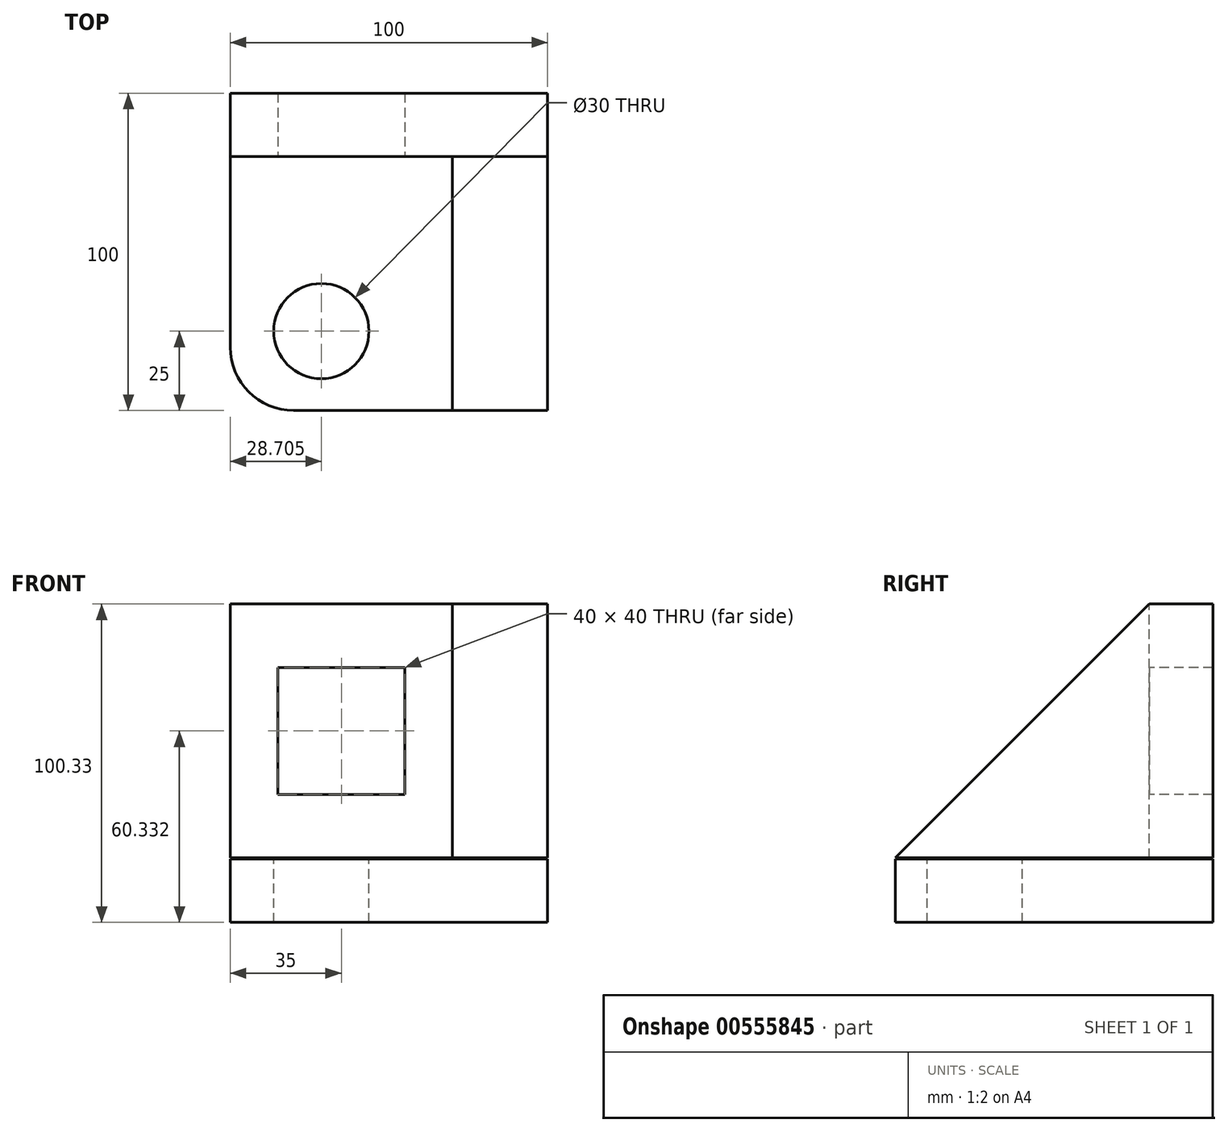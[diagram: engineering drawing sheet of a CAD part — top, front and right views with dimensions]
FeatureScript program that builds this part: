
annotation { "Feature Type Name" : "Feature", "Feature Type Description" : "" }
export const myFeature = defineFeature(function(context is Context, id is Id, definition is map)
    precondition{}
    {
        {
            var Q0;
            Q0=qCreatedBy(makeId("Top.planeOp"),FACE);
            var sketch = newSketch(context, id + "F0", { "sketchPlane" : qUnion([Q0])});
            skLineSegment(sketch, "E0.bottom", {"start": v(0, 0) * mm, "end": v(-100, 0) * mm});
            skLineSegment(sketch, "E0.top", {"start": v(0, -100) * mm, "end": v(-100, -100) * mm});
            skLineSegment(sketch, "E0.left", {"start": v(0, 0) * mm, "end": v(0, -100) * mm});
            skLineSegment(sketch, "E0.right", {"start": v(-100, 0) * mm, "end": v(-100, -100) * mm});
            skSolve(sketch);
        }
        {
            var Q0;
            Q0 = qSketchRegion(id + "F0", true);
            extrude(context, id + "F1", {"entities" : qUnion([Q0]), "depth" : 20 * mm, "offsetDistance" : 25 * mm});
        }
        {
            var Q0;
            Q0=qCreatedBy(makeId("Front.planeOp"),FACE);
            var sketch = newSketch(context, id + "F2", { "sketchPlane" : qUnion([Q0])});
            skLineSegment(sketch, "E1.bottom", {"start": v(0, 20.33) * mm, "end": v(-100, 20.33) * mm});
            skLineSegment(sketch, "E1.top", {"start": v(0, 100.33) * mm, "end": v(-100, 100.33) * mm});
            skLineSegment(sketch, "E1.left", {"start": v(0, 20.33) * mm, "end": v(0, 100.33) * mm});
            skLineSegment(sketch, "E1.right", {"start": v(-100, 20.33) * mm, "end": v(-100, 100.33) * mm});
            skSolve(sketch);
        }
        {
            var Q0;
            Q0 = qSketchRegion(id + "F2", true);
            extrude(context, id + "F3", {"entities" : qUnion([Q0]), "depth" : 20 * mm, "offsetDistance" : 25 * mm});
        }
        {
            var Q0;
            Q0=makeQuery(id+"F1.opExtrude","CAP_FACE",FACE,{"disambiguationData":[OSD([sQuery(id+"F0.wireOp",EDGE,"E0.bottom"),sQuery(id+"F0.wireOp",EDGE,"E0.top"),sQuery(id+"F0.wireOp",EDGE,"E0.left"),sQuery(id+"F0.wireOp",EDGE,"E0.right")])],"isStart":false});
            var sketch = newSketch(context, id + "F4", { "sketchPlane" : qUnion([Q0])});
            skCircle(sketch, "E2", {"center": v(-71.3, -75) * mm, "radius": 15 * mm});
            skSolve(sketch);
        }
        {
            var Q0;
            Q0 = qSketchRegion(id + "F4", true);
            extrude(context, id + "F5", {"entities" : qUnion([Q0]), "operationType" : NewBodyOperationType.REMOVE, "oppositeDirection" : true, "depth" : 22 * mm, "offsetDistance" : 25 * mm});
        }
        {
            var Q0;
            Q0=makeQuery(id+"F3.opExtrude","SWEPT_FACE",FACE,{"disambiguationData":[OSD([sQuery(id+"F2.wireOp",EDGE,"E1.left")])]});
            var sketch = newSketch(context, id + "F6", { "sketchPlane" : qUnion([Q0])});
            skLineSegment(sketch, "E3.bottom", {"start": v(-20, 20.33) * mm, "end": v(-100, 20.33) * mm});
            skLineSegment(sketch, "E3.top", {"start": v(-20, 100.33) * mm, "end": v(-100, 100.33) * mm});
            skLineSegment(sketch, "E3.left", {"start": v(-20, 20.33) * mm, "end": v(-20, 100.33) * mm});
            skLineSegment(sketch, "E3.right", {"start": v(-100, 20.33) * mm, "end": v(-100, 100.33) * mm});
            skSolve(sketch);
        }
        {
            var Q0;
            Q0 = qSketchRegion(id + "F6", true);
            extrude(context, id + "F7", {"entities" : qUnion([Q0]), "operationType" : NewBodyOperationType.ADD, "oppositeDirection" : true, "depth" : 30 * mm, "offsetDistance" : 25 * mm});
        }
        {
            var Q0;
            Q0=makeQuery(id+"F7.opExtrude","SWEPT_EDGE",EDGE,{"disambiguationData":[OSD([sQuery(id+"F6.wireOp",EDGE,"E3.top"),sQuery(id+"F6.wireOp",EDGE,"E3.right")])]});
            chamfer(context, id + "F8", {"entities" : qUnion([Q0]), "width" : 80 * mm, "tangentPropagation" : true});
        }
        {
            var Q0;
            Q0=makeQuery(id+"F1.opExtrude","SWEPT_EDGE",EDGE,{"disambiguationData":[OSD([sQuery(id+"F0.wireOp",EDGE,"E0.top"),sQuery(id+"F0.wireOp",EDGE,"E0.right")])]});
            fillet(context, id + "F9", {"entities" : qUnion([Q0]), "radius" : 20 * mm, "tangentPropagation" : true, "allowEdgeOverflow" : false});
        }
        {
            var Q0;
            Q0=makeQuery(id+"F3.opExtrude","CAP_FACE",FACE,{"disambiguationData":[OSD([sQuery(id+"F2.wireOp",EDGE,"E1.bottom"),sQuery(id+"F2.wireOp",EDGE,"E1.top"),sQuery(id+"F2.wireOp",EDGE,"E1.left"),sQuery(id+"F2.wireOp",EDGE,"E1.right")])],"isStart":false});
            var sketch = newSketch(context, id + "F10", { "sketchPlane" : qUnion([Q0])});
            skLineSegment(sketch, "E4.bottom", {"start": v(-45, 80.33) * mm, "end": v(-85, 80.33) * mm});
            skLineSegment(sketch, "E4.top", {"start": v(-45, 40.33) * mm, "end": v(-85, 40.33) * mm});
            skLineSegment(sketch, "E4.left", {"start": v(-45, 80.33) * mm, "end": v(-45, 40.33) * mm});
            skLineSegment(sketch, "E4.right", {"start": v(-85, 80.33) * mm, "end": v(-85, 40.33) * mm});
            skPoint(sketch, "E4.middle", {"position": v(-65, 60.33) * mm});
            skSolve(sketch);
        }
        {
            var Q0;
            Q0 = qSketchRegion(id + "F10", true);
            extrude(context, id + "F11", {"entities" : qUnion([Q0]), "operationType" : NewBodyOperationType.REMOVE, "oppositeDirection" : true, "depth" : 25 * mm, "offsetDistance" : 25 * mm});
        }
    });
